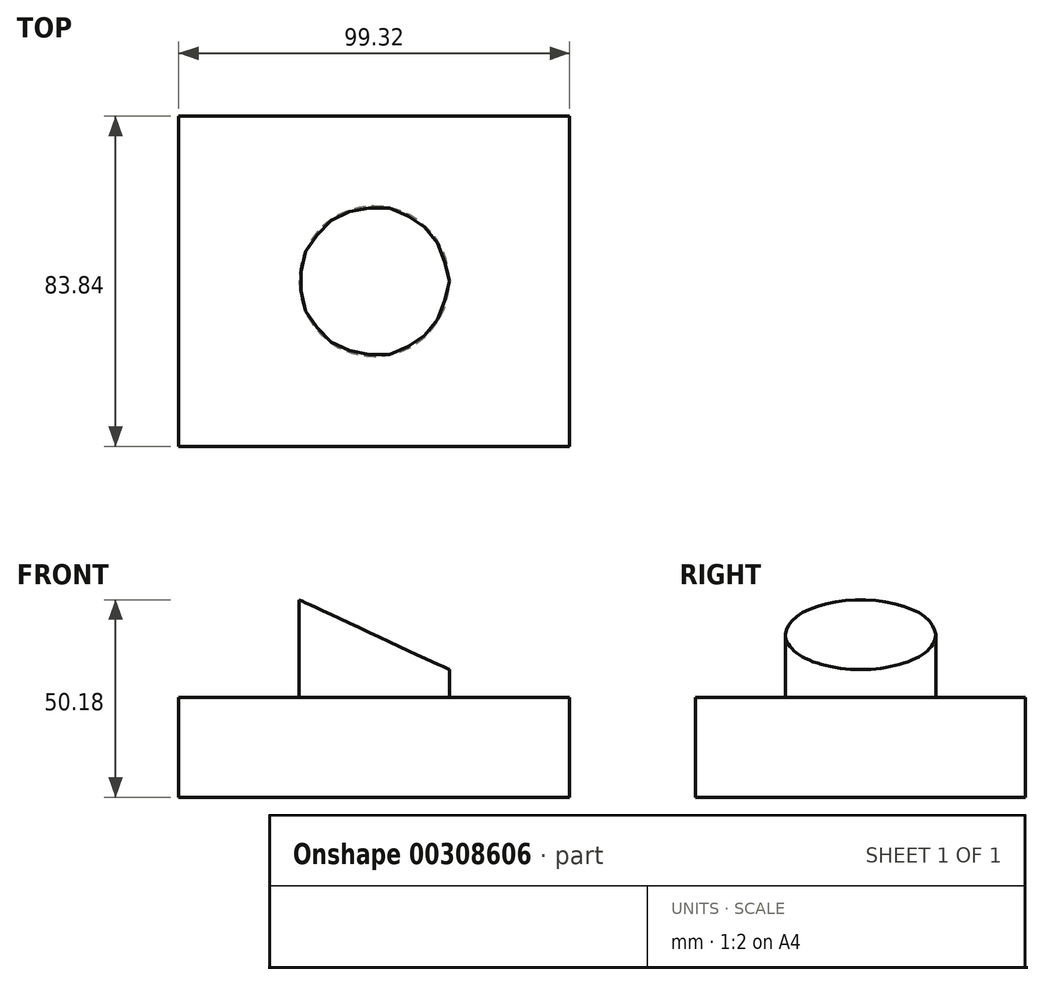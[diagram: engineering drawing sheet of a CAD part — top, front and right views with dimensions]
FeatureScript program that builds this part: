
annotation { "Feature Type Name" : "Feature", "Feature Type Description" : "" }
export const myFeature = defineFeature(function(context is Context, id is Id, definition is map)
    precondition{}
    {
        {
            var Q0;
            Q0=qCreatedBy(makeId("Top.planeOp"),FACE);
            var sketch = newSketch(context, id + "F0", { "sketchPlane" : qUnion([Q0])});
            skLineSegment(sketch, "E0.bottom", {"start": v(49.66, -41.92) * mm, "end": v(-49.66, -41.92) * mm});
            skLineSegment(sketch, "E0.top", {"start": v(49.66, 41.92) * mm, "end": v(-49.66, 41.92) * mm});
            skLineSegment(sketch, "E0.left", {"start": v(49.66, -41.92) * mm, "end": v(49.66, 41.92) * mm});
            skLineSegment(sketch, "E0.right", {"start": v(-49.66, -41.92) * mm, "end": v(-49.66, 41.92) * mm});
            skPoint(sketch, "E0.middle", {"position": v(0, 0) * mm});
            skSolve(sketch);
        }
        {
            var Q0;
            Q0=makeQuery(id+"F0.imprint","IMPRINT",FACE,{"disambiguationData":[TD([[makeQuery(id+"F0.imprint","IMPRINT",EDGE,{"derivedFrom":sQuery(id+"F0.wireOp",EDGE,"E0.bottom")}),-1.0]])]});
            extrude(context, id + "F1", {"entities" : qUnion([Q0]), "depth" : 25.4 * mm});
        }
        {
            var Q0;
            Q0=makeQuery(id+"F1.opExtrude","CAP_FACE",FACE,{"disambiguationData":[OSD([sQuery(id+"F0.wireOp",EDGE,"E0.bottom"),sQuery(id+"F0.wireOp",EDGE,"E0.top"),sQuery(id+"F0.wireOp",EDGE,"E0.left"),sQuery(id+"F0.wireOp",EDGE,"E0.right")])],"isStart":false});
            var sketch = newSketch(context, id + "F2", { "sketchPlane" : qUnion([Q0])});
            skCircle(sketch, "E1", {"center": v(0, 0) * mm, "radius": 19.1 * mm});
            skSolve(sketch);
        }
        {
            var Q0;
            Q0=makeQuery(id+"F2.imprint","IMPRINT",FACE,{"disambiguationData":[TD([[makeQuery(id+"F2.imprint","IMPRINT",EDGE,{"derivedFrom":sQuery(id+"F2.wireOp",EDGE,"E1")}),1.0]])]});
            extrude(context, id + "F3", {"entities" : qUnion([Q0]), "operationType" : NewBodyOperationType.ADD, "depth" : 25.4 * mm});
        }
        {
            var Q0;
            Q0=qCreatedBy(makeId("Front.planeOp"),FACE);
            var sketch = newSketch(context, id + "F4", { "sketchPlane" : qUnion([Q0])});
            skLineSegment(sketch, "E2", {"start": v(-26.07, 53.42) * mm, "end": v(21.9, 53.42) * mm});
            skLineSegment(sketch, "E3", {"start": v(21.9, 53.42) * mm, "end": v(21.9, 31.13) * mm});
            skLineSegment(sketch, "E4", {"start": v(21.9, 31.13) * mm, "end": v(-26.07, 53.42) * mm});
            skSolve(sketch);
        }
        {
            var Q0;
            Q0=qSketchRegion(id+"F4",true);
            extrude(context, id + "F5", {"entities" : qUnion([Q0]), "operationType" : NewBodyOperationType.REMOVE, "endBound" : BoundingType.SYMMETRIC, "depth" : 88.72 * mm});
        }
    });
